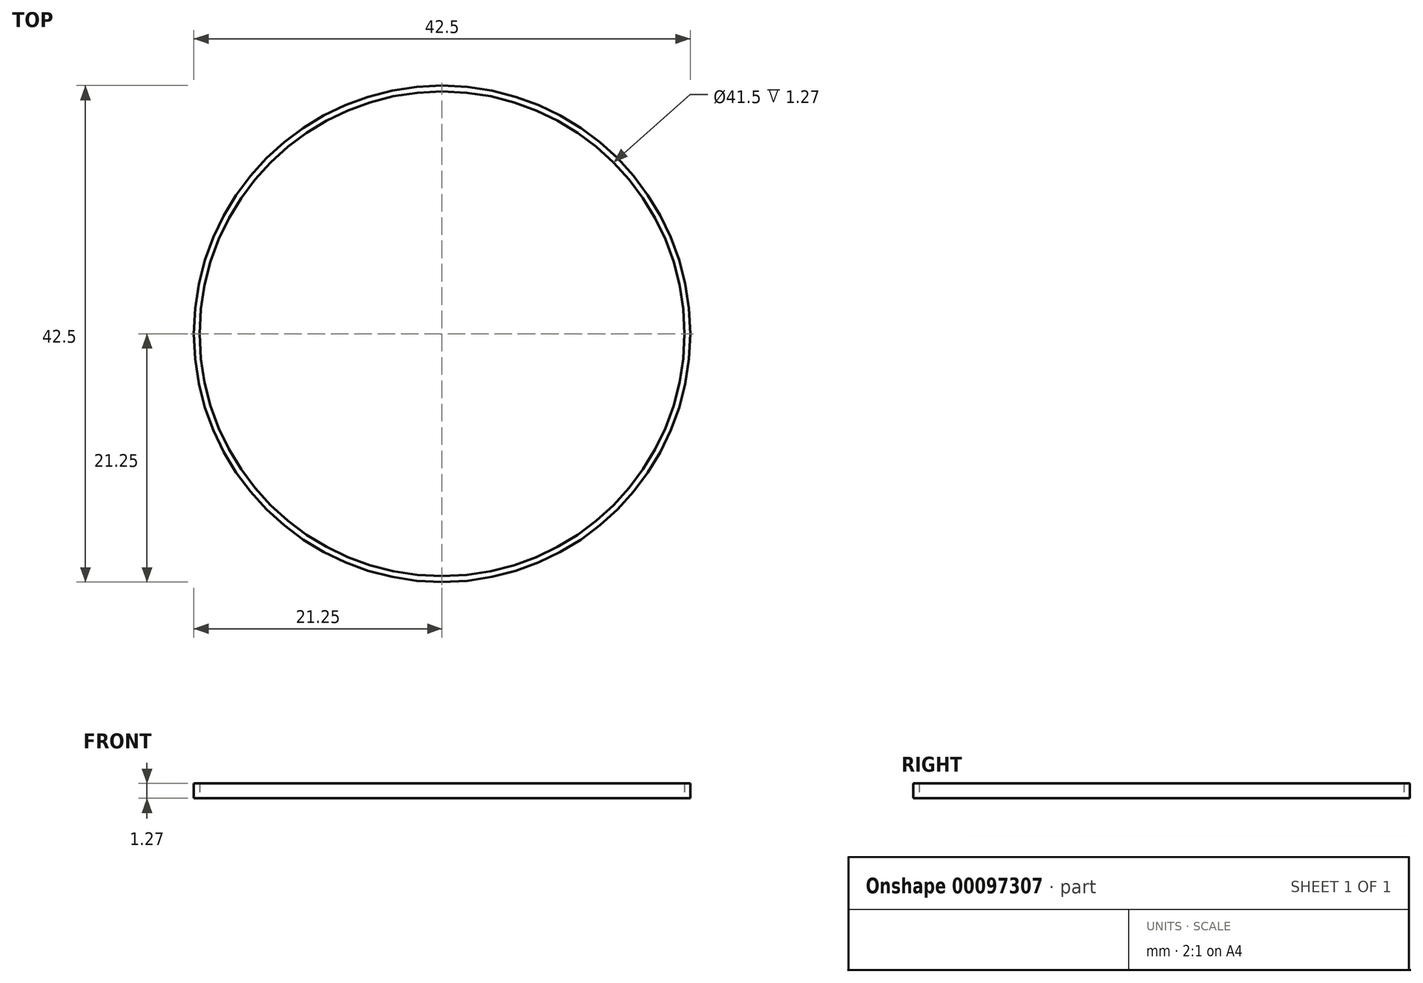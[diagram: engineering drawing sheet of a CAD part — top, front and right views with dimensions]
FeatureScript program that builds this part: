
annotation { "Feature Type Name" : "Feature", "Feature Type Description" : "" }
export const myFeature = defineFeature(function(context is Context, id is Id, definition is map)
    precondition{}
    {
        {
            var Q0;
            Q0=qCreatedBy(makeId("Top.planeOp"),FACE);
            var sketch = newSketch(context, id + "F0", { "sketchPlane" : qUnion([Q0])});
            skPoint(sketch, "E0", {"position": v(20.75, 0) * mm});
            skPoint(sketch, "E1", {"position": v(21.25, 0) * mm});
            skCircle(sketch, "E2", {"center": v(0, 0) * mm, "radius": 20.75 * mm});
            skCircle(sketch, "E3", {"center": v(0, 0) * mm, "radius": 21.25 * mm});
            skCircle(sketch, "E4", {"center": v(0, 0) * mm, "radius": 34 * mm});
            skSolve(sketch);
        }
        {
            var Q0;
            Q0=makeQuery(id+"F0.imprint","IMPRINT",FACE,{"disambiguationData":[TD([[makeQuery(id+"F0.imprint","IMPRINT",EDGE,{"derivedFrom":sQuery(id+"F0.wireOp",EDGE,"E2")}),-1.0]])]});
            extrude(context, id + "F1", {"entities" : qUnion([Q0]), "depth" : 1.27 * mm});
        }
    });
